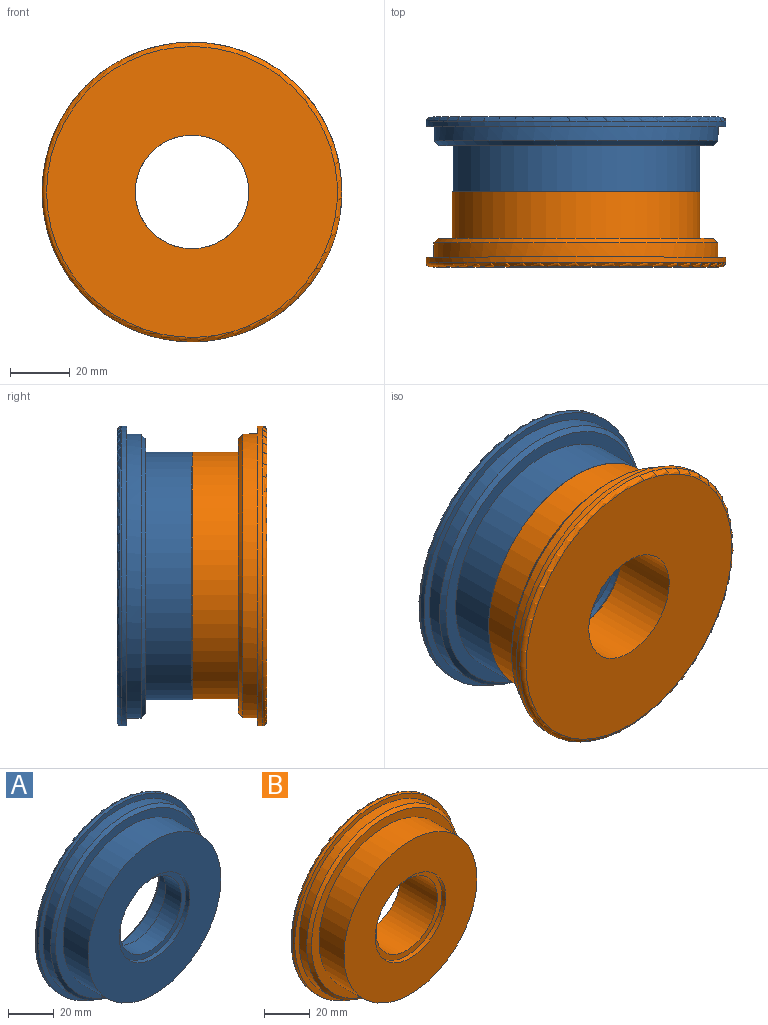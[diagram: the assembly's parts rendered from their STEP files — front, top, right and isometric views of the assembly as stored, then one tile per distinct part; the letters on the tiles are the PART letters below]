
ASSEMBLY  parts=2 mates=1
PART A: 15 faces, bbox 108.2x25x108.2 mm
  f0: cylinder r=18.95mm len=37.9mm, axis (0,1,0), area 1164.5mm2, adj f11,f13
  f1: plane 97x97mm, normal (0,1,0), area 4811.1mm2, adj f9,f14
  f2: plane 82.5x82.5mm, normal (0,-1,0), area 3842.3mm2, adj f6,f10
  f3: cylinder r=50mm len=100mm, axis (0,1,0), area 549.8mm2, adj f5,f9
  f4: cylinder r=47.38mm len=94.75mm, axis (0,-1,0), area 1413.9mm2, adj f5,f8
  f5: plane 100x100mm, normal (0,-1,0), area 803mm2, adj f3,f4
  f6: cylinder r=41.25mm len=82.5mm, axis (0,-1,0), area 4017.3mm2, adj f2,f7
  f7: plane 91.75x91.75mm, normal (0,-1,0), area 1265.9mm2, adj f6,f8
  f8: cone r=45.88mm half-angle=45deg, axis (0,1,0), area 621.4mm2, adj f4,f7
  f9: torus R=48.5mm, axis (0,-1,0), area 732.2mm2, adj f1,f3
  f10: cylinder r=21.88mm len=43.75mm, axis (0,-1,0), area 323mm2, adj f2,f11
  f11: plane 43.75x43.75mm, normal (0,-1,0), area 375.1mm2, adj f0,f10
  f12: cylinder r=27.65mm len=55.3mm, axis (0,1,0), area 2062.2mm2, adj f13,f14
  f13: plane 55.3x55.3mm, normal (0,1,0), area 1273.7mm2, adj f0,f12
  f14: torus R=28.65mm, axis (0,-1,0), area 276.5mm2, adj f1,f12
PART B: 12 faces, bbox 108.2x25x108.2 mm
  f0: cylinder r=18.95mm len=37.9mm, axis (0,1,0), area 2696.9mm2, adj f3,f11
  f1: plane 82.5x82.5mm, normal (0,-1,0), area 3842.3mm2, adj f6,f10
  f2: cylinder r=50mm len=100mm, axis (0,1,0), area 549.8mm2, adj f5,f9
  f3: plane 97x97mm, normal (0,1,0), area 6261.7mm2, adj f0,f9
  f4: cylinder r=47.38mm len=94.75mm, axis (0,-1,0), area 1413.9mm2, adj f5,f8
  f5: plane 100x100mm, normal (0,-1,0), area 803mm2, adj f2,f4
  f6: cylinder r=41.25mm len=82.5mm, axis (0,-1,0), area 4017.3mm2, adj f1,f7
  f7: plane 91.75x91.75mm, normal (0,-1,0), area 1265.9mm2, adj f6,f8
  f8: cone r=45.88mm half-angle=45deg, axis (0,1,0), area 621.4mm2, adj f4,f7
  f9: torus R=48.5mm, axis (0,-1,0), area 732.2mm2, adj f2,f3
  f10: cylinder r=21.88mm len=43.75mm, axis (0,-1,0), area 323mm2, adj f1,f11
  f11: plane 43.75x43.75mm, normal (0,-1,0), area 375.1mm2, adj f0,f10
PLACE A at identity
PLACE B rot(axis=(0.71,0,0.71),180deg) t=(0,-50,0)mm
MATE fastened B.f0 <-> A.f0  axis (0,1,0) through (0,-25,0)mm
